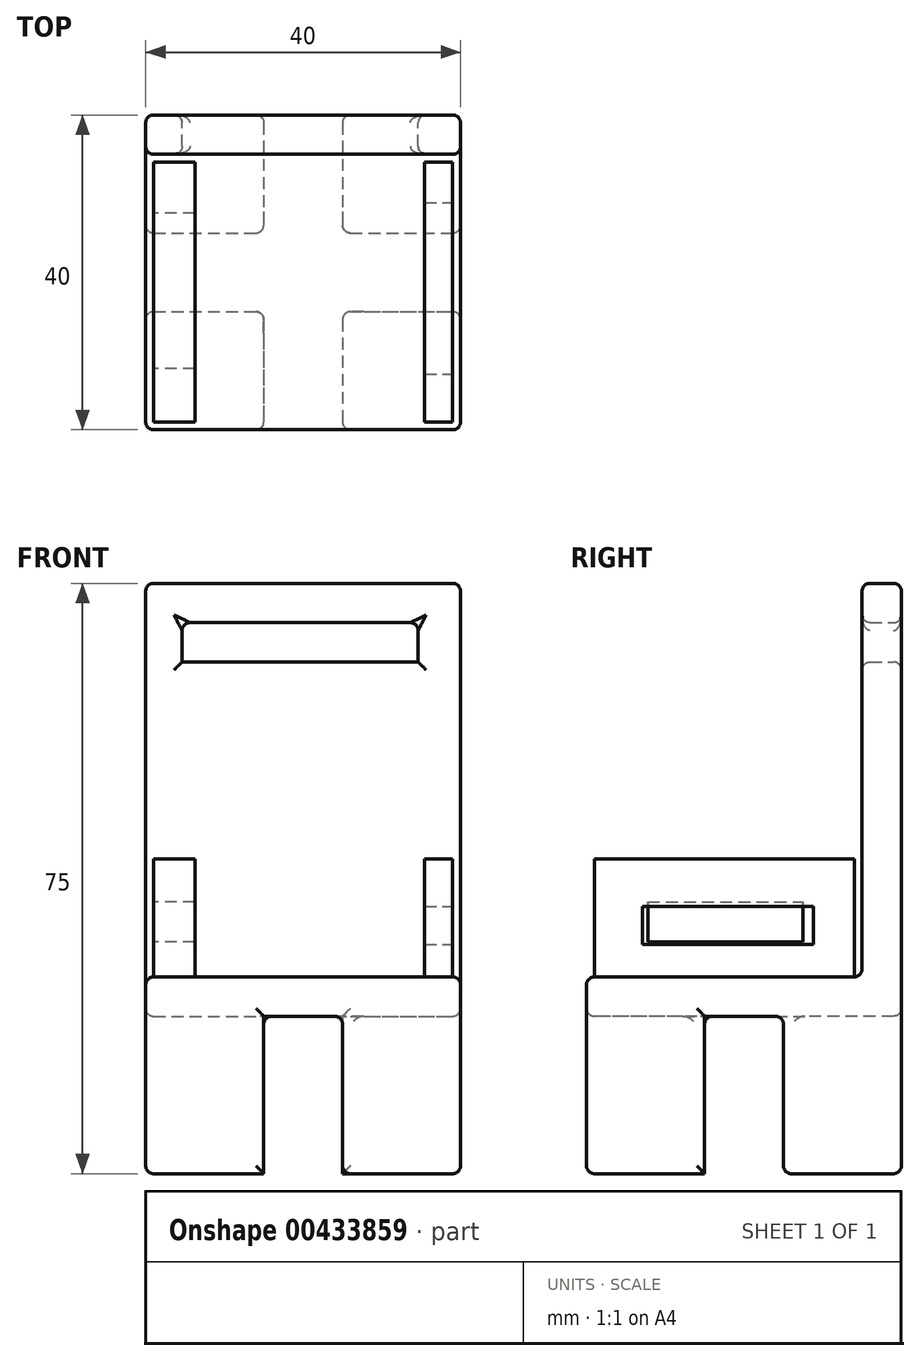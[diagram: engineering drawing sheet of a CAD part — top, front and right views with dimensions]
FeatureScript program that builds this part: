
annotation { "Feature Type Name" : "Feature", "Feature Type Description" : "" }
export const myFeature = defineFeature(function(context is Context, id is Id, definition is map)
    precondition{}
    {
        {
            var Q0;
            Q0=qCreatedBy(makeId("Top.planeOp"),FACE);
            var sketch = newSketch(context, id + "F0", { "sketchPlane" : qUnion([Q0])});
            skLineSegment(sketch, "E0.bottom", {"start": v(10, 25) * mm, "end": v(25, 25) * mm});
            skLineSegment(sketch, "E0.top", {"start": v(10, 10) * mm, "end": v(25, 10) * mm});
            skLineSegment(sketch, "E0.left", {"start": v(10, 25) * mm, "end": v(10, 10) * mm});
            skLineSegment(sketch, "E0.right", {"start": v(25, 25) * mm, "end": v(25, 10) * mm});
            skLineSegment(sketch, "E1.0.1.0", {"start": v(10, 0) * mm, "end": v(25, 0) * mm});
            skLineSegment(sketch, "E1.0.1.1", {"start": v(10, 0) * mm, "end": v(10, -15) * mm});
            skLineSegment(sketch, "E1.0.1.2", {"start": v(10, -15) * mm, "end": v(25, -15) * mm});
            skLineSegment(sketch, "E1.0.1.3", {"start": v(25, 0) * mm, "end": v(25, -15) * mm});
            skLineSegment(sketch, "E1.1.0.0", {"start": v(-15, 25) * mm, "end": v(0, 25) * mm});
            skLineSegment(sketch, "E1.1.0.1", {"start": v(-15, 25) * mm, "end": v(-15, 10) * mm});
            skLineSegment(sketch, "E1.1.0.2", {"start": v(-15, 10) * mm, "end": v(0, 10) * mm});
            skLineSegment(sketch, "E1.1.0.3", {"start": v(0, 25) * mm, "end": v(0, 10) * mm});
            skLineSegment(sketch, "E1.1.1.0", {"start": v(-15, 0) * mm, "end": v(0, 0) * mm});
            skLineSegment(sketch, "E1.1.1.1", {"start": v(-15, 0) * mm, "end": v(-15, -15) * mm});
            skLineSegment(sketch, "E1.1.1.2", {"start": v(-15, -15) * mm, "end": v(0, -15) * mm});
            skLineSegment(sketch, "E1.1.1.3", {"start": v(0, 0) * mm, "end": v(0, -15) * mm});
            skLineSegment(sketch, "E1.direction1", {"start": v(10, 25) * mm, "end": v(-15, 25) * mm, "construction": true});
            skLineSegment(sketch, "E1.direction2", {"start": v(10, 25) * mm, "end": v(10, 0) * mm, "construction": true});
            skSolve(sketch);
        }
        {
            var Q0;
            Q0=makeQuery(id+"F0.imprint","IMPRINT",FACE,{"disambiguationData":[TD([[makeQuery(id+"F0.imprint","IMPRINT",EDGE,{"derivedFrom":sQuery(id+"F0.wireOp",EDGE,"E1.1.0.0")}),-1.0]])]});
            var Q1;
            Q1=makeQuery(id+"F0.imprint","IMPRINT",FACE,{"disambiguationData":[TD([[makeQuery(id+"F0.imprint","IMPRINT",EDGE,{"derivedFrom":sQuery(id+"F0.wireOp",EDGE,"E0.bottom")}),-1.0]])]});
            var Q2;
            Q2=makeQuery(id+"F0.imprint","IMPRINT",FACE,{"disambiguationData":[TD([[makeQuery(id+"F0.imprint","IMPRINT",EDGE,{"derivedFrom":sQuery(id+"F0.wireOp",EDGE,"E1.0.1.0")}),-1.0]])]});
            var Q3;
            Q3=makeQuery(id+"F0.imprint","IMPRINT",FACE,{"disambiguationData":[TD([[makeQuery(id+"F0.imprint","IMPRINT",EDGE,{"derivedFrom":sQuery(id+"F0.wireOp",EDGE,"E1.1.1.0")}),-1.0]])]});
            extrude(context, id + "F1", {"entities" : qUnion([Q0, Q1, Q2, Q3]), "depth" : 25 * mm});
        }
        {
            var Q0;
            Q0=makeQuery(id+"F1.opExtrude","CAP_FACE",FACE,{"disambiguationData":[OSD([sQuery(id+"F0.wireOp",EDGE,"E1.1.1.0"),sQuery(id+"F0.wireOp",EDGE,"E1.1.1.1"),sQuery(id+"F0.wireOp",EDGE,"E1.1.1.2"),sQuery(id+"F0.wireOp",EDGE,"E1.1.1.3")])],"isStart":false});
            var sketch = newSketch(context, id + "F2", { "sketchPlane" : qUnion([Q0])});
            skLineSegment(sketch, "E2.bottom", {"start": v(-15, -15) * mm, "end": v(25, -15) * mm});
            skLineSegment(sketch, "E2.top", {"start": v(-15, 25) * mm, "end": v(25, 25) * mm});
            skLineSegment(sketch, "E2.left", {"start": v(-15, -15) * mm, "end": v(-15, 25) * mm});
            skLineSegment(sketch, "E2.right", {"start": v(25, -15) * mm, "end": v(25, 25) * mm});
            skSolve(sketch);
        }
        {
            var Q0;
            {var subQ3=sQuery(id+"F2.wireOp",EDGE,"E2.top");Q0=makeQuery(id+"F2.imprint","IMPRINT",FACE,{"disambiguationData":[TD([[makeQuery(id+"F2.imprint","IMPRINT",EDGE,{"derivedFrom":subQ3}),-1.0]])]});}
            var Q1;
            {var subQ4=makeQuery(id+"F1.opExtrude","CAP_EDGE",EDGE,{"disambiguationData":[OSD([sQuery(id+"F0.wireOp",EDGE,"E1.1.1.0")])],"isStart":false});Q1=makeQuery(id+"F2.imprint","IMPRINT",FACE,{"disambiguationData":[TD([[makeQuery(id+"F2.imprint","IMPRINT",EDGE,{"derivedFrom":subQ4}),-1.0]])]});}
            extrude(context, id + "F3", {"entities" : qUnion([Q0, Q1]), "operationType" : NewBodyOperationType.ADD, "oppositeDirection" : true, "depth" : 5 * mm});
        }
        {
            var Q0;
            Q0=makeQuery(id+"F3.boolean.opBoolean","MERGE",FACE,{"derivedFrom":[makeQuery(id+"F1.opExtrude","CAP_FACE",FACE,{"disambiguationData":[OSD([sQuery(id+"F0.wireOp",EDGE,"E0.bottom"),sQuery(id+"F0.wireOp",EDGE,"E0.top"),sQuery(id+"F0.wireOp",EDGE,"E0.left"),sQuery(id+"F0.wireOp",EDGE,"E0.right")])],"isStart":false}),makeQuery(id+"F1.opExtrude","CAP_FACE",FACE,{"disambiguationData":[OSD([sQuery(id+"F0.wireOp",EDGE,"E1.0.1.0"),sQuery(id+"F0.wireOp",EDGE,"E1.0.1.1"),sQuery(id+"F0.wireOp",EDGE,"E1.0.1.2"),sQuery(id+"F0.wireOp",EDGE,"E1.0.1.3")])],"isStart":false}),makeQuery(id+"F1.opExtrude","CAP_FACE",FACE,{"disambiguationData":[OSD([sQuery(id+"F0.wireOp",EDGE,"E1.1.0.0"),sQuery(id+"F0.wireOp",EDGE,"E1.1.0.1"),sQuery(id+"F0.wireOp",EDGE,"E1.1.0.2"),sQuery(id+"F0.wireOp",EDGE,"E1.1.0.3")])],"isStart":false}),makeQuery(id+"F1.opExtrude","CAP_FACE",FACE,{"disambiguationData":[OSD([sQuery(id+"F0.wireOp",EDGE,"E1.1.1.0"),sQuery(id+"F0.wireOp",EDGE,"E1.1.1.1"),sQuery(id+"F0.wireOp",EDGE,"E1.1.1.2"),sQuery(id+"F0.wireOp",EDGE,"E1.1.1.3")])],"isStart":false}),makeQuery(id+"F3.opExtrude","CAP_FACE",FACE,{"disambiguationData":[OSD([sQuery(id+"F2.wireOp",EDGE,"E2.bottom"),sQuery(id+"F2.wireOp",EDGE,"E2.top"),sQuery(id+"F2.wireOp",EDGE,"E2.left"),sQuery(id+"F2.wireOp",EDGE,"E2.right")])],"isStart":true})]});
            var sketch = newSketch(context, id + "F4", { "sketchPlane" : qUnion([Q0])});
            skLineSegment(sketch, "E3.bottom", {"start": v(-15, 25) * mm, "end": v(25, 25) * mm});
            skLineSegment(sketch, "E3.top", {"start": v(-15, 20) * mm, "end": v(25, 20) * mm});
            skLineSegment(sketch, "E3.left", {"start": v(-15, 25) * mm, "end": v(-15, 20) * mm});
            skLineSegment(sketch, "E3.right", {"start": v(25, 25) * mm, "end": v(25, 20) * mm});
            skSolve(sketch);
        }
        {
            var Q0;
            Q0 = qSketchRegion(id + "F4", true);
            extrude(context, id + "F5", {"entities" : qUnion([Q0]), "operationType" : NewBodyOperationType.ADD, "depth" : 50 * mm});
        }
        {
            var Q0;
            Q0=makeQuery(id+"F5.boolean.opBoolean","MERGE",FACE,{"derivedFrom":[makeQuery(id+"F3.boolean.opBoolean","MERGE",FACE,{"derivedFrom":[makeQuery(id+"F1.opExtrude","SWEPT_FACE",FACE,{"disambiguationData":[OSD([sQuery(id+"F0.wireOp",EDGE,"E0.bottom")])]}),makeQuery(id+"F1.opExtrude","SWEPT_FACE",FACE,{"disambiguationData":[OSD([sQuery(id+"F0.wireOp",EDGE,"E1.1.0.0")])]}),makeQuery(id+"F3.opExtrude","SWEPT_FACE",FACE,{"disambiguationData":[OSD([sQuery(id+"F2.wireOp",EDGE,"E2.top")])]})]}),makeQuery(id+"F5.opExtrude","SWEPT_FACE",FACE,{"disambiguationData":[OSD([sQuery(id+"F4.wireOp",EDGE,"E3.bottom")])]})]});
            var sketch = newSketch(context, id + "F6", { "sketchPlane" : qUnion([Q0])});
            skLineSegment(sketch, "E4.bottom", {"start": v(10.38, 70) * mm, "end": v(-19.62, 70) * mm});
            skLineSegment(sketch, "E4.top", {"start": v(10.38, 65) * mm, "end": v(-19.62, 65) * mm});
            skLineSegment(sketch, "E4.left", {"start": v(10.38, 70) * mm, "end": v(10.38, 65) * mm});
            skLineSegment(sketch, "E4.right", {"start": v(-19.62, 70) * mm, "end": v(-19.62, 65) * mm});
            skSolve(sketch);
        }
        {
            var Q0;
            Q0 = qSketchRegion(id + "F6", true);
            extrude(context, id + "F7", {"entities" : qUnion([Q0]), "operationType" : NewBodyOperationType.REMOVE, "oppositeDirection" : true, "depth" : 25 * mm});
        }
        {
            var Q0;
            Q0=makeQuery(id+"F5.opExtrude","SWEPT_EDGE",EDGE,{"disambiguationData":[OSD([sQuery(id+"F0.wireOp",EDGE,"E1.1.0.1"),sQuery(id+"F0.wireOp",EDGE,"E1.1.1.1"),sQuery(id+"F2.wireOp",EDGE,"E2.left"),sQuery(id+"F4.wireOp",EDGE,"E3.top"),sQuery(id+"F4.wireOp",EDGE,"E3.left")])]});
            var Q1;
            Q1=makeQuery(id+"F5.opExtrude","SWEPT_FACE",FACE,{"disambiguationData":[OSD([sQuery(id+"F4.wireOp",EDGE,"E3.top")])]});
            var Q2;
            Q2=makeQuery(id+"F3.boolean.opBoolean","MERGE",FACE,{"derivedFrom":[makeQuery(id+"F1.opExtrude","SWEPT_FACE",FACE,{"disambiguationData":[OSD([sQuery(id+"F0.wireOp",EDGE,"E1.0.1.2")])]}),makeQuery(id+"F1.opExtrude","SWEPT_FACE",FACE,{"disambiguationData":[OSD([sQuery(id+"F0.wireOp",EDGE,"E1.1.1.2")])]}),makeQuery(id+"F3.opExtrude","SWEPT_FACE",FACE,{"disambiguationData":[OSD([sQuery(id+"F2.wireOp",EDGE,"E2.bottom")])]})]});
            var Q3;
            Q3=makeQuery(id+"F3.boolean.opBoolean","MERGE",FACE,{"derivedFrom":[makeQuery(id+"F1.opExtrude","CAP_FACE",FACE,{"disambiguationData":[OSD([sQuery(id+"F0.wireOp",EDGE,"E0.bottom"),sQuery(id+"F0.wireOp",EDGE,"E0.top"),sQuery(id+"F0.wireOp",EDGE,"E0.left"),sQuery(id+"F0.wireOp",EDGE,"E0.right")])],"isStart":false}),makeQuery(id+"F1.opExtrude","CAP_FACE",FACE,{"disambiguationData":[OSD([sQuery(id+"F0.wireOp",EDGE,"E1.0.1.0"),sQuery(id+"F0.wireOp",EDGE,"E1.0.1.1"),sQuery(id+"F0.wireOp",EDGE,"E1.0.1.2"),sQuery(id+"F0.wireOp",EDGE,"E1.0.1.3")])],"isStart":false}),makeQuery(id+"F1.opExtrude","CAP_FACE",FACE,{"disambiguationData":[OSD([sQuery(id+"F0.wireOp",EDGE,"E1.1.0.0"),sQuery(id+"F0.wireOp",EDGE,"E1.1.0.1"),sQuery(id+"F0.wireOp",EDGE,"E1.1.0.2"),sQuery(id+"F0.wireOp",EDGE,"E1.1.0.3")])],"isStart":false}),makeQuery(id+"F1.opExtrude","CAP_FACE",FACE,{"disambiguationData":[OSD([sQuery(id+"F0.wireOp",EDGE,"E1.1.1.0"),sQuery(id+"F0.wireOp",EDGE,"E1.1.1.1"),sQuery(id+"F0.wireOp",EDGE,"E1.1.1.2"),sQuery(id+"F0.wireOp",EDGE,"E1.1.1.3")])],"isStart":false}),makeQuery(id+"F3.opExtrude","CAP_FACE",FACE,{"disambiguationData":[OSD([sQuery(id+"F2.wireOp",EDGE,"E2.bottom"),sQuery(id+"F2.wireOp",EDGE,"E2.top"),sQuery(id+"F2.wireOp",EDGE,"E2.left"),sQuery(id+"F2.wireOp",EDGE,"E2.right")])],"isStart":true})]});
            var Q4;
            Q4=makeQuery(id+"F5.boolean.opBoolean","MERGE",FACE,{"derivedFrom":[makeQuery(id+"F3.boolean.opBoolean","MERGE",FACE,{"derivedFrom":[makeQuery(id+"F1.opExtrude","SWEPT_FACE",FACE,{"disambiguationData":[OSD([sQuery(id+"F0.wireOp",EDGE,"E0.right")])]}),makeQuery(id+"F1.opExtrude","SWEPT_FACE",FACE,{"disambiguationData":[OSD([sQuery(id+"F0.wireOp",EDGE,"E1.0.1.3")])]}),makeQuery(id+"F3.opExtrude","SWEPT_FACE",FACE,{"disambiguationData":[OSD([sQuery(id+"F2.wireOp",EDGE,"E2.right")])]})]}),makeQuery(id+"F5.opExtrude","SWEPT_FACE",FACE,{"disambiguationData":[OSD([sQuery(id+"F4.wireOp",EDGE,"E3.right")])]})]});
            var Q5;
            Q5=makeQuery(id+"F1.opExtrude","SWEPT_EDGE",EDGE,{"disambiguationData":[OSD([sQuery(id+"F0.wireOp",EDGE,"E1.0.1.0"),sQuery(id+"F0.wireOp",EDGE,"E1.0.1.1")])]});
            var Q6;
            Q6=makeQuery(id+"F1.opExtrude","SWEPT_FACE",FACE,{"disambiguationData":[OSD([sQuery(id+"F0.wireOp",EDGE,"E1.1.1.0")])]});
            var Q7;
            Q7=makeQuery(id+"F5.boolean.opBoolean","MERGE",FACE,{"derivedFrom":[makeQuery(id+"F3.boolean.opBoolean","MERGE",FACE,{"derivedFrom":[makeQuery(id+"F1.opExtrude","SWEPT_FACE",FACE,{"disambiguationData":[OSD([sQuery(id+"F0.wireOp",EDGE,"E0.bottom")])]}),makeQuery(id+"F1.opExtrude","SWEPT_FACE",FACE,{"disambiguationData":[OSD([sQuery(id+"F0.wireOp",EDGE,"E1.1.0.0")])]}),makeQuery(id+"F3.opExtrude","SWEPT_FACE",FACE,{"disambiguationData":[OSD([sQuery(id+"F2.wireOp",EDGE,"E2.top")])]})]}),makeQuery(id+"F5.opExtrude","SWEPT_FACE",FACE,{"disambiguationData":[OSD([sQuery(id+"F4.wireOp",EDGE,"E3.bottom")])]})]});
            var Q8;
            Q8=makeQuery(id+"F5.boolean.opBoolean","MERGE",FACE,{"derivedFrom":[makeQuery(id+"F3.boolean.opBoolean","MERGE",FACE,{"derivedFrom":[makeQuery(id+"F1.opExtrude","SWEPT_FACE",FACE,{"disambiguationData":[OSD([sQuery(id+"F0.wireOp",EDGE,"E1.1.0.1")])]}),makeQuery(id+"F1.opExtrude","SWEPT_FACE",FACE,{"disambiguationData":[OSD([sQuery(id+"F0.wireOp",EDGE,"E1.1.1.1")])]}),makeQuery(id+"F3.opExtrude","SWEPT_FACE",FACE,{"disambiguationData":[OSD([sQuery(id+"F2.wireOp",EDGE,"E2.left")])]})]}),makeQuery(id+"F5.opExtrude","SWEPT_FACE",FACE,{"disambiguationData":[OSD([sQuery(id+"F4.wireOp",EDGE,"E3.left")])]})]});
            var Q9;
            Q9=makeQuery(id+"F1.opExtrude","SWEPT_FACE",FACE,{"disambiguationData":[OSD([sQuery(id+"F0.wireOp",EDGE,"E1.0.1.1")])]});
            var Q10;
            Q10=makeQuery(id+"F1.opExtrude","SWEPT_EDGE",EDGE,{"disambiguationData":[OSD([sQuery(id+"F0.wireOp",EDGE,"E1.1.1.2"),sQuery(id+"F0.wireOp",EDGE,"E1.1.1.3")])]});
            var Q11;
            Q11=makeQuery(id+"F1.opExtrude","SWEPT_FACE",FACE,{"disambiguationData":[OSD([sQuery(id+"F0.wireOp",EDGE,"E0.top")])]});
            var Q12;
            Q12=makeQuery(id+"F1.opExtrude","SWEPT_FACE",FACE,{"disambiguationData":[OSD([sQuery(id+"F0.wireOp",EDGE,"E1.1.0.2")])]});
            fillet(context, id + "F8", {"entities" : qUnion([Q0, Q1, Q2, Q3, Q4, Q5, Q6, Q7, Q8, Q9, Q10, Q11, Q12]), "radius" : 1 * mm, "tangentPropagation" : true, "allowEdgeOverflow" : false});
        }
        {
            var Q0;
            Q0=makeQuery(id+"F8.opFillet","BLEND_FACE",FACE,{"disambiguationData":[OSD([sQuery(id+"F4.wireOp",EDGE,"E3.top"),sQuery(id+"F6.wireOp",EDGE,"E4.bottom")])]});
            var Q1;
            {var subQ0=makeQuery(id+"F7.opExtrude","SWEPT_FACE",FACE,{"disambiguationData":[OSD([sQuery(id+"F6.wireOp",EDGE,"E4.top")])]});Q1=makeQuery(id+"F8.opFillet","BLEND_EDGE",EDGE,{"blendedFrom":[makeQuery(id+"F7.boolean.opBoolean","INTERSECT",EDGE,{"derivedFrom":[makeQuery(id+"F5.opExtrude","SWEPT_FACE",FACE,{"disambiguationData":[OSD([sQuery(id+"F4.wireOp",EDGE,"E3.top")])]}),subQ0]}),makeQuery(id+"F7.boolean.opBoolean","COPY",FACE,{"derivedFrom":subQ0})],"blendedInto":[makeQuery(id+"F7.boolean.opBoolean","COPY",FACE,{"derivedFrom":subQ0})]});}
            var Q2;
            {var subQ0=makeQuery(id+"F7.opExtrude","SWEPT_FACE",FACE,{"disambiguationData":[OSD([sQuery(id+"F6.wireOp",EDGE,"E4.right")])]});Q2=makeQuery(id+"F8.opFillet","BLEND_EDGE",EDGE,{"blendedFrom":[makeQuery(id+"F7.boolean.opBoolean","INTERSECT",EDGE,{"derivedFrom":[makeQuery(id+"F5.opExtrude","SWEPT_FACE",FACE,{"disambiguationData":[OSD([sQuery(id+"F4.wireOp",EDGE,"E3.top")])]}),subQ0]}),makeQuery(id+"F7.boolean.opBoolean","COPY",FACE,{"derivedFrom":subQ0})],"blendedInto":[makeQuery(id+"F7.boolean.opBoolean","COPY",FACE,{"derivedFrom":subQ0})]});}
            var Q3;
            {var subQ0=makeQuery(id+"F7.opExtrude","SWEPT_FACE",FACE,{"disambiguationData":[OSD([sQuery(id+"F6.wireOp",EDGE,"E4.left")])]});Q3=makeQuery(id+"F8.opFillet","BLEND_EDGE",EDGE,{"blendedFrom":[makeQuery(id+"F7.boolean.opBoolean","INTERSECT",EDGE,{"derivedFrom":[makeQuery(id+"F5.opExtrude","SWEPT_FACE",FACE,{"disambiguationData":[OSD([sQuery(id+"F4.wireOp",EDGE,"E3.top")])]}),subQ0]}),makeQuery(id+"F7.boolean.opBoolean","COPY",FACE,{"derivedFrom":subQ0})],"blendedInto":[makeQuery(id+"F7.boolean.opBoolean","COPY",FACE,{"derivedFrom":subQ0})]});}
            fillet(context, id + "F9", {"entities" : qUnion([Q0, Q1, Q2, Q3]), "radius" : 1 * mm, "tangentPropagation" : true, "allowEdgeOverflow" : false});
        }
        {
            var Q0;
            Q0=makeQuery(id+"F3.boolean.opBoolean","MERGE",FACE,{"derivedFrom":[makeQuery(id+"F1.opExtrude","CAP_FACE",FACE,{"disambiguationData":[OSD([sQuery(id+"F0.wireOp",EDGE,"E0.bottom"),sQuery(id+"F0.wireOp",EDGE,"E0.top"),sQuery(id+"F0.wireOp",EDGE,"E0.left"),sQuery(id+"F0.wireOp",EDGE,"E0.right")])],"isStart":false}),makeQuery(id+"F1.opExtrude","CAP_FACE",FACE,{"disambiguationData":[OSD([sQuery(id+"F0.wireOp",EDGE,"E1.0.1.0"),sQuery(id+"F0.wireOp",EDGE,"E1.0.1.1"),sQuery(id+"F0.wireOp",EDGE,"E1.0.1.2"),sQuery(id+"F0.wireOp",EDGE,"E1.0.1.3")])],"isStart":false}),makeQuery(id+"F1.opExtrude","CAP_FACE",FACE,{"disambiguationData":[OSD([sQuery(id+"F0.wireOp",EDGE,"E1.1.0.0"),sQuery(id+"F0.wireOp",EDGE,"E1.1.0.1"),sQuery(id+"F0.wireOp",EDGE,"E1.1.0.2"),sQuery(id+"F0.wireOp",EDGE,"E1.1.0.3")])],"isStart":false}),makeQuery(id+"F1.opExtrude","CAP_FACE",FACE,{"disambiguationData":[OSD([sQuery(id+"F0.wireOp",EDGE,"E1.1.1.0"),sQuery(id+"F0.wireOp",EDGE,"E1.1.1.1"),sQuery(id+"F0.wireOp",EDGE,"E1.1.1.2"),sQuery(id+"F0.wireOp",EDGE,"E1.1.1.3")])],"isStart":false}),makeQuery(id+"F3.opExtrude","CAP_FACE",FACE,{"disambiguationData":[OSD([sQuery(id+"F2.wireOp",EDGE,"E2.bottom"),sQuery(id+"F2.wireOp",EDGE,"E2.top"),sQuery(id+"F2.wireOp",EDGE,"E2.left"),sQuery(id+"F2.wireOp",EDGE,"E2.right")])],"isStart":true})]});
            var sketch = newSketch(context, id + "F10", { "sketchPlane" : qUnion([Q0])});
            skLineSegment(sketch, "E5.bottom", {"start": v(24, 19) * mm, "end": v(20.43, 19) * mm});
            skLineSegment(sketch, "E5.top", {"start": v(24, -14) * mm, "end": v(20.43, -14) * mm});
            skLineSegment(sketch, "E5.left", {"start": v(24, 19) * mm, "end": v(24, -14) * mm});
            skLineSegment(sketch, "E5.right", {"start": v(20.43, 19) * mm, "end": v(20.43, -14) * mm});
            skSolve(sketch);
        }
        {
            var Q0;
            Q0 = qSketchRegion(id + "F10", true);
            extrude(context, id + "F11", {"entities" : qUnion([Q0]), "operationType" : NewBodyOperationType.ADD, "depth" : 15 * mm});
        }
        {
            var Q0;
            Q0=makeQuery(id+"F11.opExtrude","SWEPT_FACE",FACE,{"disambiguationData":[OSD([sQuery(id+"F10.wireOp",EDGE,"E5.left")])]});
            var sketch = newSketch(context, id + "F12", { "sketchPlane" : qUnion([Q0])});
            skLineSegment(sketch, "E6.bottom", {"start": v(13.84, 33.95) * mm, "end": v(-7.91, 33.95) * mm});
            skLineSegment(sketch, "E6.top", {"start": v(13.84, 29.11) * mm, "end": v(-7.91, 29.11) * mm});
            skLineSegment(sketch, "E6.left", {"start": v(13.84, 33.95) * mm, "end": v(13.84, 29.11) * mm});
            skLineSegment(sketch, "E6.right", {"start": v(-7.91, 33.95) * mm, "end": v(-7.91, 29.11) * mm});
            skSolve(sketch);
        }
        {
            var Q0;
            Q0 = qSketchRegion(id + "F12", true);
            extrude(context, id + "F13", {"entities" : qUnion([Q0]), "operationType" : NewBodyOperationType.REMOVE, "oppositeDirection" : true, "depth" : 25 * mm});
        }
        {
            var Q0;
            Q0=makeQuery(id+"F3.boolean.opBoolean","MERGE",FACE,{"derivedFrom":[makeQuery(id+"F1.opExtrude","CAP_FACE",FACE,{"disambiguationData":[OSD([sQuery(id+"F0.wireOp",EDGE,"E0.bottom"),sQuery(id+"F0.wireOp",EDGE,"E0.top"),sQuery(id+"F0.wireOp",EDGE,"E0.left"),sQuery(id+"F0.wireOp",EDGE,"E0.right")])],"isStart":false}),makeQuery(id+"F1.opExtrude","CAP_FACE",FACE,{"disambiguationData":[OSD([sQuery(id+"F0.wireOp",EDGE,"E1.0.1.0"),sQuery(id+"F0.wireOp",EDGE,"E1.0.1.1"),sQuery(id+"F0.wireOp",EDGE,"E1.0.1.2"),sQuery(id+"F0.wireOp",EDGE,"E1.0.1.3")])],"isStart":false}),makeQuery(id+"F1.opExtrude","CAP_FACE",FACE,{"disambiguationData":[OSD([sQuery(id+"F0.wireOp",EDGE,"E1.1.0.0"),sQuery(id+"F0.wireOp",EDGE,"E1.1.0.1"),sQuery(id+"F0.wireOp",EDGE,"E1.1.0.2"),sQuery(id+"F0.wireOp",EDGE,"E1.1.0.3")])],"isStart":false}),makeQuery(id+"F1.opExtrude","CAP_FACE",FACE,{"disambiguationData":[OSD([sQuery(id+"F0.wireOp",EDGE,"E1.1.1.0"),sQuery(id+"F0.wireOp",EDGE,"E1.1.1.1"),sQuery(id+"F0.wireOp",EDGE,"E1.1.1.2"),sQuery(id+"F0.wireOp",EDGE,"E1.1.1.3")])],"isStart":false}),makeQuery(id+"F3.opExtrude","CAP_FACE",FACE,{"disambiguationData":[OSD([sQuery(id+"F2.wireOp",EDGE,"E2.bottom"),sQuery(id+"F2.wireOp",EDGE,"E2.top"),sQuery(id+"F2.wireOp",EDGE,"E2.left"),sQuery(id+"F2.wireOp",EDGE,"E2.right")])],"isStart":true})]});
            var sketch = newSketch(context, id + "F14", { "sketchPlane" : qUnion([Q0])});
            skLineSegment(sketch, "E7.bottom", {"start": v(-14, 19) * mm, "end": v(-8.76, 19) * mm});
            skLineSegment(sketch, "E7.top", {"start": v(-14, -14) * mm, "end": v(-8.76, -14) * mm});
            skLineSegment(sketch, "E7.left", {"start": v(-14, 19) * mm, "end": v(-14, -14) * mm});
            skLineSegment(sketch, "E7.right", {"start": v(-8.76, 19) * mm, "end": v(-8.76, -14) * mm});
            skSolve(sketch);
        }
        {
            var Q0;
            Q0=makeQuery(id+"F14.imprint","IMPRINT",FACE,{"disambiguationData":[TD([[makeQuery(id+"F14.imprint","IMPRINT",EDGE,{"derivedFrom":sQuery(id+"F14.wireOp",EDGE,"E7.bottom")}),1.0]])]});
            extrude(context, id + "F15", {"entities" : qUnion([Q0]), "operationType" : NewBodyOperationType.ADD, "depth" : 15 * mm});
        }
        {
            var Q0;
            Q0=makeQuery(id+"F15.opExtrude","SWEPT_FACE",FACE,{"disambiguationData":[OSD([sQuery(id+"F14.wireOp",EDGE,"E7.left")])]});
            var sketch = newSketch(context, id + "F16", { "sketchPlane" : qUnion([Q0])});
            skLineSegment(sketch, "E8.bottom", {"start": v(-12.5, 34.53) * mm, "end": v(7.21, 34.53) * mm});
            skLineSegment(sketch, "E8.top", {"start": v(-12.5, 29.43) * mm, "end": v(7.21, 29.43) * mm});
            skLineSegment(sketch, "E8.left", {"start": v(-12.5, 34.53) * mm, "end": v(-12.5, 29.43) * mm});
            skLineSegment(sketch, "E8.right", {"start": v(7.21, 34.53) * mm, "end": v(7.21, 29.43) * mm});
            skSolve(sketch);
        }
        {
            var Q0;
            Q0 = qSketchRegion(id + "F16", true);
            extrude(context, id + "F17", {"entities" : qUnion([Q0]), "operationType" : NewBodyOperationType.REMOVE, "oppositeDirection" : true, "depth" : 25 * mm});
        }
    });
